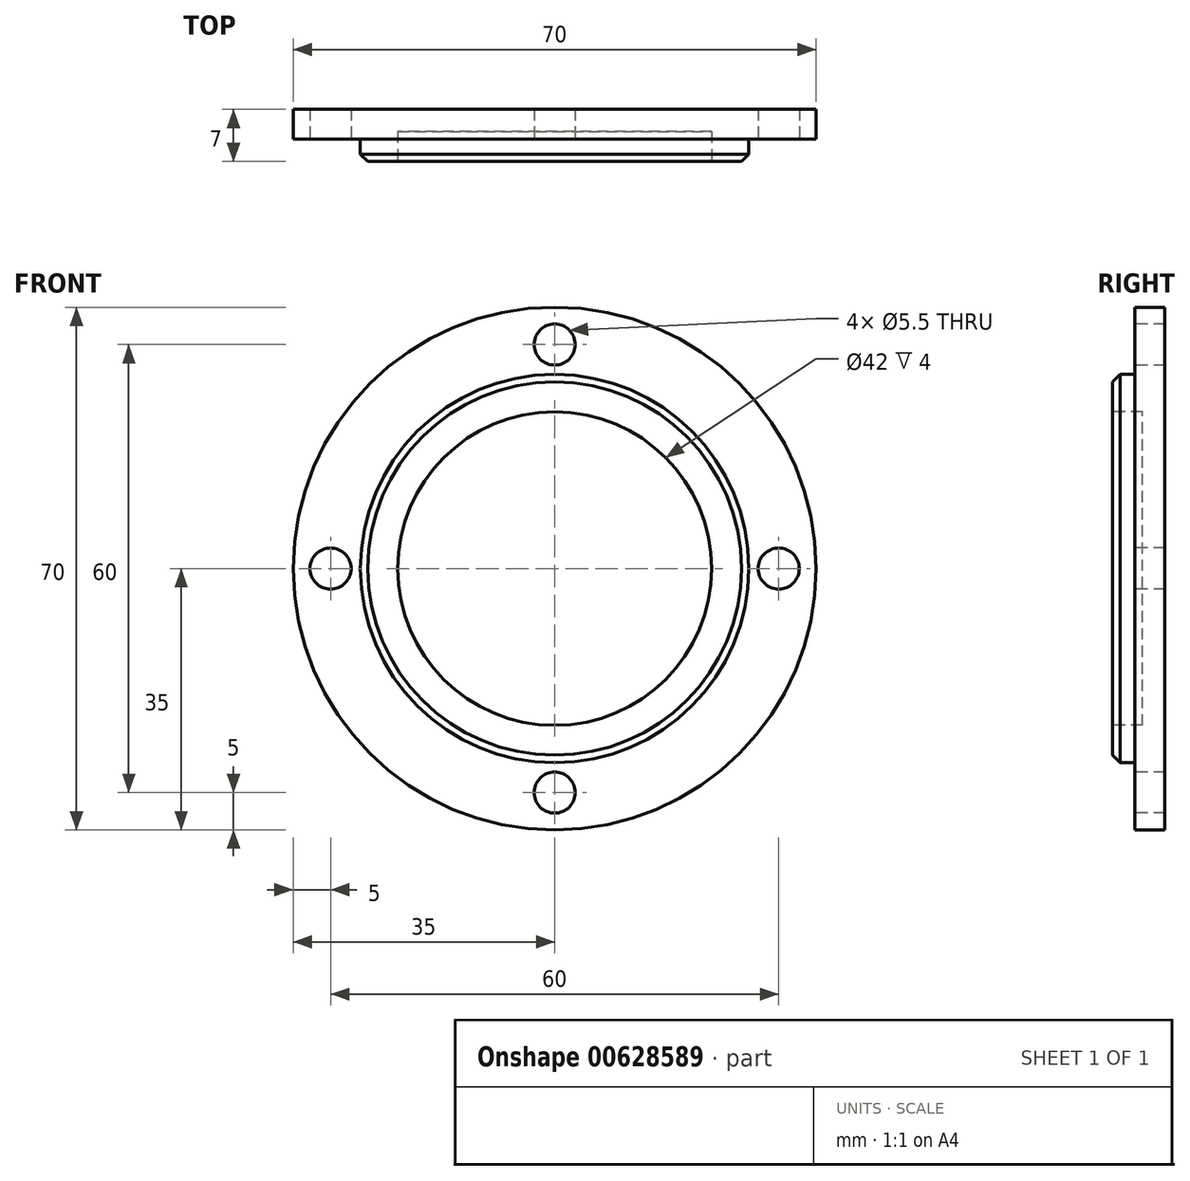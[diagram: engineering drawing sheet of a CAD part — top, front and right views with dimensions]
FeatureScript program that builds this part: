
annotation { "Feature Type Name" : "Feature", "Feature Type Description" : "" }
export const myFeature = defineFeature(function(context is Context, id is Id, definition is map)
    precondition{}
    {
        {
            var Q0;
            Q0=qCreatedBy(makeId("Front.planeOp"),FACE);
            var sketch = newSketch(context, id + "F0", { "sketchPlane" : qUnion([Q0])});
            skCircle(sketch, "E0", {"center": v(0, 0) * mm, "radius": 35 * mm});
            skSolve(sketch);
        }
        {
            var Q0;
            Q0 = qSketchRegion(id + "F0", true);
            extrude(context, id + "F1", {"entities" : qUnion([Q0]), "depth" : 4 * mm, "offsetDistance" : 25 * mm});
        }
        {
            var Q0;
            Q0=makeQuery(id+"F1.opExtrude","CAP_FACE",FACE,{"disambiguationData":[OSD([sQuery(id+"F0.wireOp",EDGE,"E0")])],"isStart":false});
            var sketch = newSketch(context, id + "F2", { "sketchPlane" : qUnion([Q0])});
            skCircle(sketch, "E1", {"center": v(0, 0) * mm, "radius": 30 * mm, "construction": true});
            skLineSegment(sketch, "E2", {"start": v(0, 0) * mm, "end": v(73.77, 0) * mm, "construction": true});
            skLineSegment(sketch, "E3", {"start": v(0, 0) * mm, "end": v(0, 62.04) * mm, "construction": true});
            skCircle(sketch, "E4", {"center": v(30, 0) * mm, "radius": 2.75 * mm});
            skCircle(sketch, "E5", {"center": v(0, 30) * mm, "radius": 2.75 * mm});
            skCircle(sketch, "E6.MirrorC", {"center": v(-30, 0) * mm, "radius": 2.75 * mm});
            skCircle(sketch, "E7.MirrorC", {"center": v(0, -30) * mm, "radius": 2.75 * mm});
            skSolve(sketch);
        }
        {
            var Q0;
            Q0 = qSketchRegion(id + "F2", true);
            extrude(context, id + "F3", {"entities" : qUnion([Q0]), "operationType" : NewBodyOperationType.REMOVE, "endBound" : BoundingType.UP_TO_NEXT, "oppositeDirection" : true, "depth" : 25 * mm, "offsetDistance" : 25 * mm});
        }
        {
            var Q0;
            Q0=makeQuery(id+"F1.opExtrude","CAP_FACE",FACE,{"disambiguationData":[OSD([sQuery(id+"F0.wireOp",EDGE,"E0")])],"isStart":false});
            var sketch = newSketch(context, id + "F4", { "sketchPlane" : qUnion([Q0])});
            skCircle(sketch, "E8", {"center": v(0, 0) * mm, "radius": 26 * mm});
            skSolve(sketch);
        }
        {
            var Q0;
            Q0 = qSketchRegion(id + "F4", true);
            extrude(context, id + "F5", {"entities" : qUnion([Q0]), "operationType" : NewBodyOperationType.ADD, "depth" : 3 * mm, "offsetDistance" : 25 * mm});
        }
        {
            var Q0;
            Q0=makeQuery(id+"F5.opExtrude","CAP_FACE",FACE,{"disambiguationData":[OSD([sQuery(id+"F4.wireOp",EDGE,"E8")])],"isStart":false});
            var sketch = newSketch(context, id + "F6", { "sketchPlane" : qUnion([Q0])});
            skCircle(sketch, "E9", {"center": v(0, 0) * mm, "radius": 21 * mm});
            skSolve(sketch);
        }
        {
            var Q0;
            Q0 = qSketchRegion(id + "F6", true);
            extrude(context, id + "F7", {"entities" : qUnion([Q0]), "operationType" : NewBodyOperationType.REMOVE, "oppositeDirection" : true, "depth" : 4 * mm, "offsetDistance" : 25 * mm});
        }
        {
            var Q0;
            Q0=makeQuery(id+"F5.opExtrude","CAP_EDGE",EDGE,{"disambiguationData":[OSD([sQuery(id+"F4.wireOp",EDGE,"E8")])],"isStart":false});
            chamfer(context, id + "F8", {"entities" : qUnion([Q0]), "width" : 1 * mm, "tangentPropagation" : true});
        }
    });
